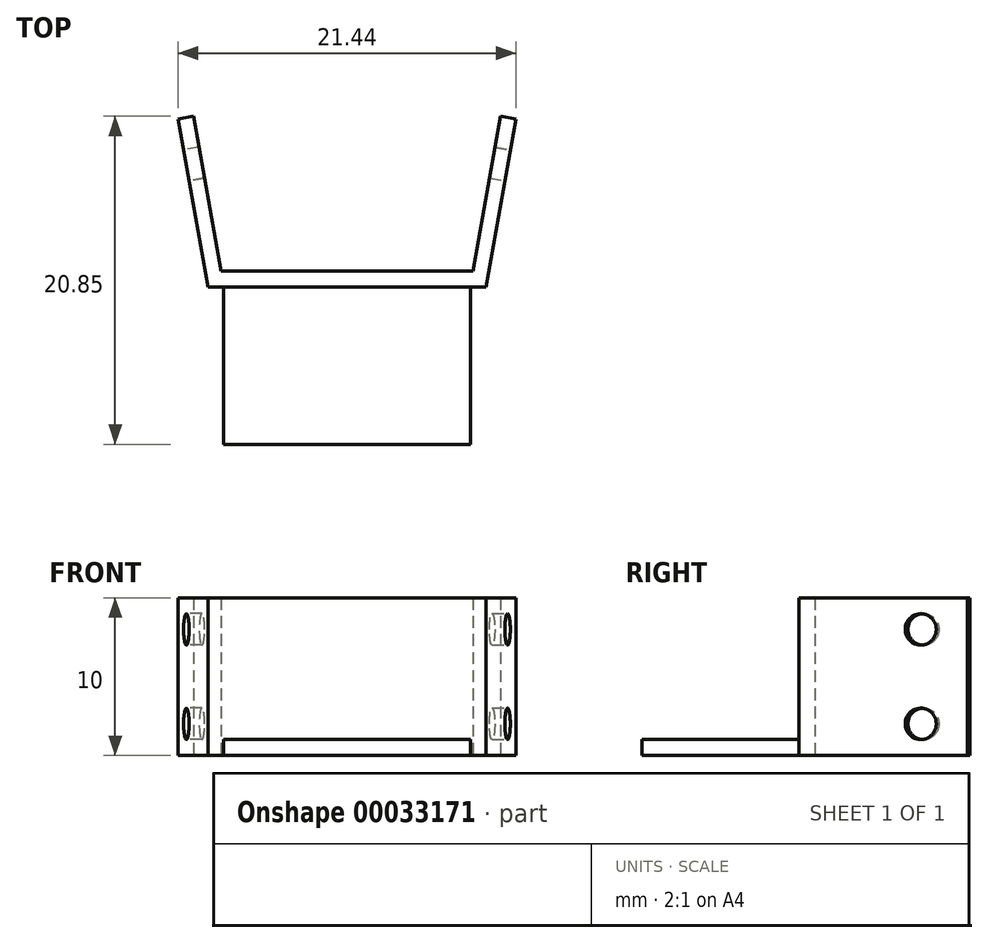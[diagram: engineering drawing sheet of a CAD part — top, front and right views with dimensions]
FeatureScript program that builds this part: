
annotation { "Feature Type Name" : "Feature", "Feature Type Description" : "" }
export const myFeature = defineFeature(function(context is Context, id is Id, definition is map)
    precondition{}
    {
        {
            var Q0;
            Q0=qCreatedBy(makeId("Top.planeOp"),FACE);
            var sketch = newSketch(context, id + "F0", { "sketchPlane" : qUnion([Q0])});
            skLineSegment(sketch, "E0", {"start": v(0, 0) * mm, "end": v(8, 0) * mm});
            skLineSegment(sketch, "E1", {"start": v(8, 0) * mm, "end": v(9.74, 9.85) * mm});
            skLineSegment(sketch, "E2", {"start": v(9.74, 9.85) * mm, "end": v(10.72, 9.67) * mm});
            skLineSegment(sketch, "E3", {"start": v(10.72, 9.67) * mm, "end": v(8.84, -1) * mm});
            skLineSegment(sketch, "E4", {"start": v(8.84, -1) * mm, "end": v(0, -1) * mm});
            skLineSegment(sketch, "E5.MirrorCS", {"start": v(0, 0) * mm, "end": v(-8, 0) * mm});
            skLineSegment(sketch, "E6.MirrorCS", {"start": v(-8.84, -1) * mm, "end": v(0, -1) * mm});
            skLineSegment(sketch, "E7.MirrorCS", {"start": v(-10.72, 9.67) * mm, "end": v(-8.84, -1) * mm});
            skLineSegment(sketch, "E8.MirrorCS", {"start": v(-8, 0) * mm, "end": v(-9.74, 9.85) * mm});
            skLineSegment(sketch, "E9.MirrorCS", {"start": v(-9.74, 9.85) * mm, "end": v(-10.72, 9.67) * mm});
            skSolve(sketch);
        }
        {
            var Q0;
            Q0 = qSketchRegion(id + "F0", true);
            extrude(context, id + "F1", {"entities" : qUnion([Q0]), "depth" : 10 * mm});
        }
        {
            var Q0;
            Q0=makeQuery(id+"F1.opExtrude","SWEPT_FACE",FACE,{"disambiguationData":[OSD([sQuery(id+"F0.wireOp",EDGE,"E7.MirrorCS")])]});
            var sketch = newSketch(context, id + "F2", { "sketchPlane" : qUnion([Q0])});
            skLineSegment(sketch, "E10", {"start": v(-11.39, 5) * mm, "end": v(-0.55, 5) * mm, "construction": true});
            skCircle(sketch, "E11", {"center": v(-8.39, 8) * mm, "radius": 1 * mm});
            skCircle(sketch, "E12.MirrorC", {"center": v(-8.39, 2) * mm, "radius": 1 * mm});
            skSolve(sketch);
        }
        {
            var Q0;
            Q0 = qSketchRegion(id + "F2", true);
            extrude(context, id + "F3", {"entities" : qUnion([Q0]), "operationType" : NewBodyOperationType.REMOVE, "endBound" : BoundingType.UP_TO_NEXT, "oppositeDirection" : true, "depth" : 25 * mm});
        }
        {
            var Q0;
            Q0=makeQuery(id+"F1.opExtrude","SWEPT_FACE",FACE,{"disambiguationData":[OSD([sQuery(id+"F0.wireOp",EDGE,"E3")])]});
            var sketch = newSketch(context, id + "F4", { "sketchPlane" : qUnion([Q0])});
            skLineSegment(sketch, "E13", {"start": v(0.55, 5) * mm, "end": v(11.39, 5) * mm, "construction": true});
            skCircle(sketch, "E14", {"center": v(8.39, 8) * mm, "radius": 1 * mm});
            skCircle(sketch, "E15.MirrorC", {"center": v(8.39, 2) * mm, "radius": 1 * mm});
            skSolve(sketch);
        }
        {
            var Q0;
            Q0 = qSketchRegion(id + "F4", true);
            extrude(context, id + "F5", {"entities" : qUnion([Q0]), "operationType" : NewBodyOperationType.REMOVE, "endBound" : BoundingType.UP_TO_NEXT, "oppositeDirection" : true, "depth" : 25 * mm});
        }
        {
            var Q0;
            Q0=makeQuery(id+"F1.opExtrude","SWEPT_FACE",FACE,{"disambiguationData":[OSD([sQuery(id+"F0.wireOp",EDGE,"E4"),sQuery(id+"F0.wireOp",EDGE,"E6.MirrorCS")])]});
            var sketch = newSketch(context, id + "F6", { "sketchPlane" : qUnion([Q0])});
            skLineSegment(sketch, "E16.bottom", {"start": v(7.84, 1) * mm, "end": v(-7.84, 1) * mm});
            skLineSegment(sketch, "E16.left", {"start": v(7.84, 1) * mm, "end": v(7.84, 0) * mm});
            skLineSegment(sketch, "E16.right", {"start": v(-7.84, 1) * mm, "end": v(-7.84, 0) * mm});
            skPoint(sketch, "E16.middle", {"position": v(0, 0) * mm});
            skLineSegment(sketch, "E17", {"start": v(-7.84, 0) * mm, "end": v(7.84, 0) * mm});
            skPoint(sketch, "E16.top.end.orphan", {"position": v(-7.84, -1) * mm});
            skPoint(sketch, "E18.orphan", {"position": v(7.84, -1) * mm});
            skSolve(sketch);
        }
        {
            var Q0;
            Q0 = qSketchRegion(id + "F6", true);
            extrude(context, id + "F7", {"entities" : qUnion([Q0]), "operationType" : NewBodyOperationType.ADD, "depth" : 10 * mm});
        }
    });
